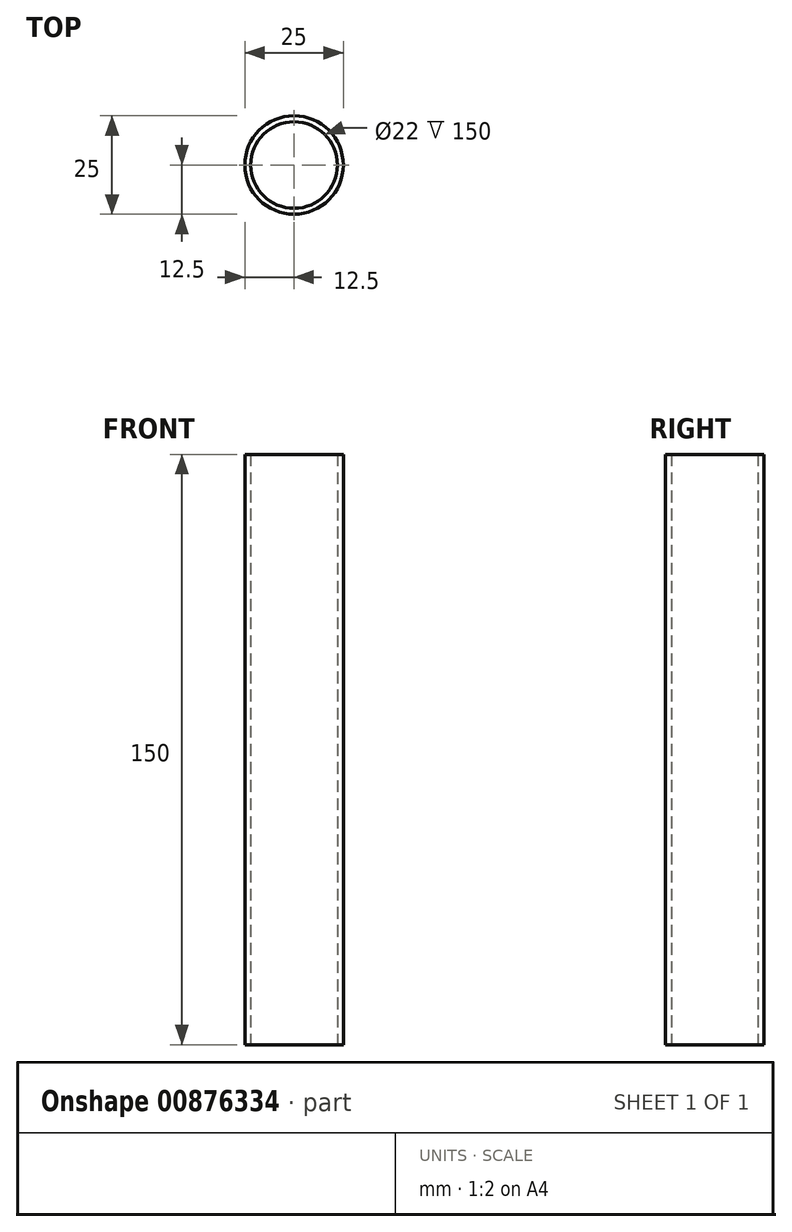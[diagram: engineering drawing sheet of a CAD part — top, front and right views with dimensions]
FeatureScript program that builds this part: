
annotation { "Feature Type Name" : "Feature", "Feature Type Description" : "" }
export const myFeature = defineFeature(function(context is Context, id is Id, definition is map)
    precondition{}
    {
        {
            var Q0;
            Q0=qCreatedBy(makeId("Top.planeOp"),FACE);
            var sketch = newSketch(context, id + "F0", { "sketchPlane" : qUnion([Q0])});
            skCircle(sketch, "E0", {"center": v(0, 0) * mm, "radius": 12.5 * mm});
            skCircle(sketch, "E1", {"center": v(0, 0) * mm, "radius": 11 * mm});
            skSolve(sketch);
        }
        {
            var Q0;
            Q0=qCreatedBy(makeId("Front.planeOp"),FACE);
            var sketch = newSketch(context, id + "F1", { "sketchPlane" : qUnion([Q0])});
            skLineSegment(sketch, "E2", {"start": v(0, 0) * mm, "end": v(0, -150) * mm});
            skSolve(sketch);
        }
        {
            var Q0;
            Q0=makeQuery(id+"F0.imprint","IMPRINT",FACE,{"disambiguationData":[TD([[makeQuery(id+"F0.imprint","IMPRINT",EDGE,{"derivedFrom":sQuery(id+"F0.wireOp",EDGE,"E0")}),1.0]])]});
            var Q1;
            Q1=sQuery(id+"F1.wireOp",EDGE,"E2");
            sweep(context, id + "F2", {"profiles" : qUnion([Q0]), "path" : qUnion([Q1])});
        }
    });
